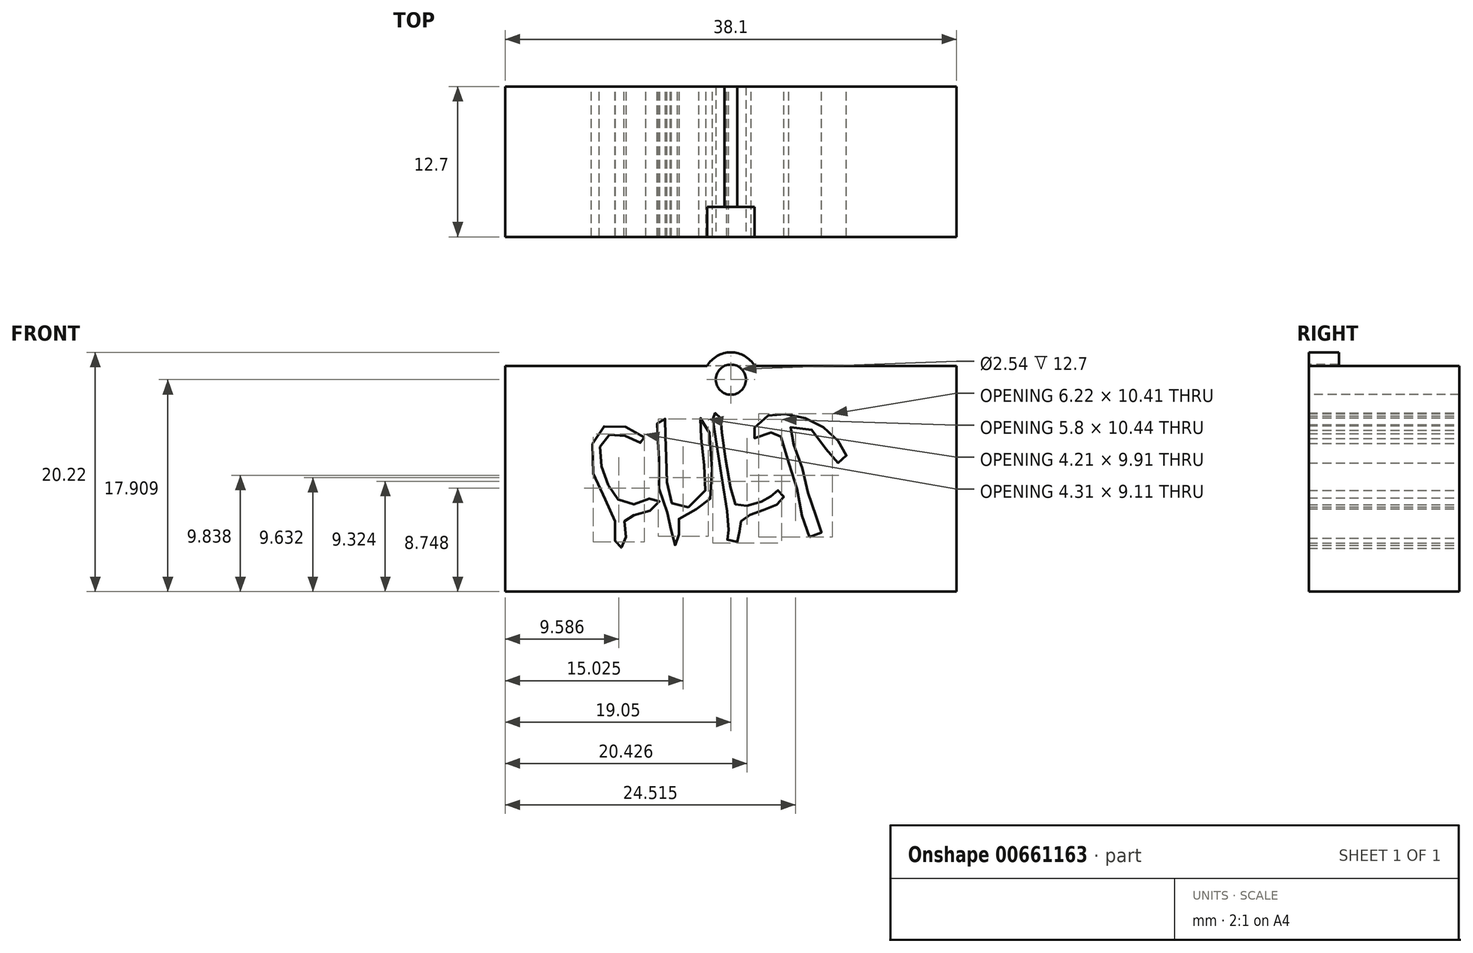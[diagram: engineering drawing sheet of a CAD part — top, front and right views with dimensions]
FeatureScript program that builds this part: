
annotation { "Feature Type Name" : "Feature", "Feature Type Description" : "" }
export const myFeature = defineFeature(function(context is Context, id is Id, definition is map)
    precondition{}
    {
        {
            var Q0;
            Q0=qCreatedBy(makeId("Front.planeOp"),FACE);
            var sketch = newSketch(context, id + "F0", { "sketchPlane" : qUnion([Q0])});
            skLineSegment(sketch, "E0.bottom", {"start": v(19.05, 9.53) * mm, "end": v(-19.05, 9.53) * mm});
            skLineSegment(sketch, "E0.top", {"start": v(19.05, -9.53) * mm, "end": v(-19.05, -9.53) * mm});
            skLineSegment(sketch, "E0.left", {"start": v(19.05, 9.53) * mm, "end": v(19.05, -9.53) * mm});
            skLineSegment(sketch, "E0.right", {"start": v(-19.05, 9.53) * mm, "end": v(-19.05, -9.53) * mm});
            skPoint(sketch, "E0.middle", {"position": v(0, 0) * mm});
            skSolve(sketch);
        }
        {
            var Q0;
            Q0=makeQuery(id+"F0.imprint","IMPRINT",FACE,{"disambiguationData":[TD([[makeQuery(id+"F0.imprint","IMPRINT",EDGE,{"derivedFrom":sQuery(id+"F0.wireOp",EDGE,"E0.bottom")}),1.0]])]});
            extrude(context, id + "F1", {"entities" : qUnion([Q0]), "depth" : 12.7 * mm, "offsetDistance" : 25.4 * mm});
        }
        {
            var Q0;
            Q0=makeQuery(id+"F1.opExtrude","CAP_FACE",FACE,{"disambiguationData":[OSD([sQuery(id+"F0.wireOp",EDGE,"E0.bottom"),sQuery(id+"F0.wireOp",EDGE,"E0.top"),sQuery(id+"F0.wireOp",EDGE,"E0.left"),sQuery(id+"F0.wireOp",EDGE,"E0.right")])],"isStart":false});
            var sketch = newSketch(context, id + "F2", { "sketchPlane" : qUnion([Q0])});
            skFitSpline(sketch, "E1", {"points": [v(-7.3, 3.52) * mm, v(-9.58, 4.55) * mm, v(-11.33, 3.88) * mm, v(-11.5, 0) * mm, v(-9.86, -3.22) * mm, v(-9.78, -5.25) * mm, v(-9.5, -5.85) * mm, v(-8.9, -5.53) * mm, v(-8.9, -4.61) * mm, v(-8.94, -3.42) * mm, v(-8.34, -3.1) * mm, v(-7.07, -2.78) * mm, v(-6, -2.06) * mm, v(-6.4, -1.63) * mm, v(-7.1, -1.74) * mm, v(-8.54, -2.18) * mm, v(-9.78, -1.47) * mm, v(-10.58, 0) * mm, v(-11.1, 2.04) * mm, v(-10.66, 3.48) * mm, v(-9.46, 3.8) * mm, v(-8.19, 3.28) * mm, v(-7.27, 3.04) * mm, v(-7.3, 3.52) * mm]});
            skSolve(sketch);
        }
        {
            var Q0;
            Q0=makeQuery(id+"F2.imprint","IMPRINT",FACE,{"disambiguationData":[TD([[makeQuery(id+"F2.imprint","IMPRINT",EDGE,{"derivedFrom":sQuery(id+"F2.wireOp",EDGE,"E1")}),1.0]])]});
            extrude(context, id + "F3", {"entities" : qUnion([Q0]), "operationType" : NewBodyOperationType.REMOVE, "oppositeDirection" : true, "depth" : 25.4 * mm, "offsetDistance" : 25.4 * mm});
        }
        {
            var Q0;
            Q0=makeQuery(id+"F1.opExtrude","CAP_FACE",FACE,{"disambiguationData":[OSD([sQuery(id+"F0.wireOp",EDGE,"E0.bottom"),sQuery(id+"F0.wireOp",EDGE,"E0.top"),sQuery(id+"F0.wireOp",EDGE,"E0.left"),sQuery(id+"F0.wireOp",EDGE,"E0.right")])],"isStart":false});
            var sketch = newSketch(context, id + "F4", { "sketchPlane" : qUnion([Q0])});
            skFitSpline(sketch, "E2", {"points": [v(-5.37, -2.83) * mm, v(-5, -3.96) * mm, v(-5.06, -5.29) * mm, v(-4.5, -5.6) * mm, v(-4.36, -4.95) * mm, v(-4.5, -4.02) * mm, v(-4.22, -3.14) * mm, v(-2.64, -2.47) * mm, v(-1.8, -1.82) * mm, v(-1.62, 1.65) * mm, v(-2.21, 5.06) * mm, v(-2.64, 5.06) * mm, v(-2.47, 3.28) * mm, v(-2.19, 0.5) * mm, v(-2.41, -1.6) * mm, v(-4.38, -2.52) * mm, v(-5.06, -1.88) * mm, v(-5.43, 0) * mm, v(-5.48, 2.24) * mm, v(-5.51, 3.87) * mm, v(-5.48, 4.97) * mm, v(-6.02, 5.28) * mm, v(-6.22, 4.35) * mm, v(-6.16, 3.17) * mm, v(-6.05, 2.44) * mm, v(-6.1, -0.4) * mm, v(-5.37, -2.83) * mm]});
            skSolve(sketch);
        }
        {
            var Q0;
            Q0=makeQuery(id+"F4.imprint","IMPRINT",FACE,{"disambiguationData":[TD([[makeQuery(id+"F4.imprint","IMPRINT",EDGE,{"derivedFrom":sQuery(id+"F4.wireOp",EDGE,"E2")}),1.0]])]});
            extrude(context, id + "F5", {"entities" : qUnion([Q0]), "operationType" : NewBodyOperationType.REMOVE, "oppositeDirection" : true, "depth" : 25.4 * mm, "offsetDistance" : 25.4 * mm});
        }
        {
            var Q0;
            Q0=makeQuery(id+"F1.opExtrude","CAP_FACE",FACE,{"disambiguationData":[OSD([sQuery(id+"F0.wireOp",EDGE,"E0.bottom"),sQuery(id+"F0.wireOp",EDGE,"E0.top"),sQuery(id+"F0.wireOp",EDGE,"E0.left"),sQuery(id+"F0.wireOp",EDGE,"E0.right")])],"isStart":false});
            var sketch = newSketch(context, id + "F6", { "sketchPlane" : qUnion([Q0])});
            skFitSpline(sketch, "E3", {"points": [v(-1.53, 5.01) * mm, v(-0.51, -1.6) * mm, v(-0.23, -4.51) * mm, v(-0.31, -5.1) * mm, v(0.42, -5.41) * mm, v(0.73, -4.74) * mm, v(0.76, -4.06) * mm, v(0.98, -3.38) * mm, v(1.89, -2.93) * mm, v(3.24, -2.45) * mm, v(4.25, -1.92) * mm, v(4.45, -1.36) * mm, v(4, -0.96) * mm, v(3.52, -1.3) * mm, v(3.04, -1.75) * mm, v(1.86, -2.14) * mm, v(0.59, -2.31) * mm, v(0, -0.9) * mm, v(-0.76, 4.06) * mm, v(-0.9, 5.24) * mm, v(-1.22, 5.58) * mm, v(-1.53, 5.4) * mm, v(-1.53, 5.01) * mm]});
            skSolve(sketch);
        }
        {
            var Q0;
            Q0=makeQuery(id+"F6.imprint","IMPRINT",FACE,{"disambiguationData":[TD([[makeQuery(id+"F6.imprint","IMPRINT",EDGE,{"derivedFrom":sQuery(id+"F6.wireOp",EDGE,"E3")}),1.0]])]});
            extrude(context, id + "F7", {"entities" : qUnion([Q0]), "operationType" : NewBodyOperationType.REMOVE, "oppositeDirection" : true, "depth" : 25.4 * mm, "offsetDistance" : 25.4 * mm});
        }
        {
            var Q0;
            Q0=makeQuery(id+"F1.opExtrude","CAP_FACE",FACE,{"disambiguationData":[OSD([sQuery(id+"F0.wireOp",EDGE,"E0.bottom"),sQuery(id+"F0.wireOp",EDGE,"E0.top"),sQuery(id+"F0.wireOp",EDGE,"E0.left"),sQuery(id+"F0.wireOp",EDGE,"E0.right")])],"isStart":false});
            var sketch = newSketch(context, id + "F8", { "sketchPlane" : qUnion([Q0])});
            skFitSpline(sketch, "E4", {"points": [v(6.64, -4.9) * mm, v(7.58, -4.7) * mm, v(7.35, -3.52) * mm, v(6.4, -0.73) * mm, v(5.55, 2.35) * mm, v(4.98, 4.3) * mm, v(7.16, 3.92) * mm, v(8.48, 1.69) * mm, v(9.53, 1.4) * mm, v(9.72, 2.21) * mm, v(8.67, 3.59) * mm, v(7.1, 4.82) * mm, v(5.02, 5.39) * mm, v(3.37, 5.43) * mm, v(2.09, 4.44) * mm, v(1.75, 3.54) * mm, v(3.03, 3.63) * mm, v(3.84, 4.1) * mm, v(4.88, 1.36) * mm, v(5.83, -1.96) * mm, v(6.64, -4.9) * mm]});
            skSolve(sketch);
        }
        {
            var Q0;
            Q0=makeQuery(id+"F8.imprint","IMPRINT",FACE,{"disambiguationData":[TD([[makeQuery(id+"F8.imprint","IMPRINT",EDGE,{"derivedFrom":sQuery(id+"F8.wireOp",EDGE,"E4")}),1.0]])]});
            extrude(context, id + "F9", {"entities" : qUnion([Q0]), "operationType" : NewBodyOperationType.REMOVE, "oppositeDirection" : true, "depth" : 25.4 * mm, "offsetDistance" : 25.4 * mm});
        }
        {
            var Q0;
            Q0=makeQuery(id+"F1.opExtrude","CAP_FACE",FACE,{"disambiguationData":[OSD([sQuery(id+"F0.wireOp",EDGE,"E0.bottom"),sQuery(id+"F0.wireOp",EDGE,"E0.top"),sQuery(id+"F0.wireOp",EDGE,"E0.left"),sQuery(id+"F0.wireOp",EDGE,"E0.right")])],"isStart":false});
            var sketch = newSketch(context, id + "F10", { "sketchPlane" : qUnion([Q0])});
            skCircle(sketch, "E5", {"center": v(0, 8.38) * mm, "radius": 2.3 * mm});
            skSolve(sketch);
        }
        {
            var Q0;
            {var subQ0=sQuery(id+"F10.wireOp",EDGE,"E5");var subQ1=makeQuery(id+"F1.opExtrude","CAP_EDGE",EDGE,{"disambiguationData":[OSD([sQuery(id+"F0.wireOp",EDGE,"E0.bottom")])],"isStart":false});var subQ2=makeQuery(id+"F10.imprint","INTERSECT",VERTEX,{"disambiguationData":[OD(0.0)],"derivedFrom":[subQ1,subQ0]});Q0=makeQuery(id+"F10.imprint","IMPRINT",FACE,{"disambiguationData":[TD([[makeQuery(id+"F10.imprint","IMPRINT",EDGE,{"disambiguationData":[TD([[subQ2,-1.0]])],"derivedFrom":subQ0}),1.0]])]});}
            extrude(context, id + "F11", {"entities" : qUnion([Q0]), "operationType" : NewBodyOperationType.ADD, "oppositeDirection" : true, "depth" : 2.54 * mm, "offsetDistance" : 25.4 * mm});
        }
        {
            var Q0;
            {var subQ0=sQuery(id+"F0.wireOp",EDGE,"E0.bottom");Q0=makeQuery(id+"F11.boolean.opBoolean","MERGE",FACE,{"derivedFrom":[makeQuery(id+"F1.opExtrude","CAP_FACE",FACE,{"disambiguationData":[OSD([subQ0,sQuery(id+"F0.wireOp",EDGE,"E0.top"),sQuery(id+"F0.wireOp",EDGE,"E0.left"),sQuery(id+"F0.wireOp",EDGE,"E0.right")])],"isStart":false}),makeQuery(id+"F11.opExtrude","CAP_FACE",FACE,{"disambiguationData":[OSD([subQ0,sQuery(id+"F10.wireOp",EDGE,"E5")])],"isStart":true})]});}
            var sketch = newSketch(context, id + "F12", { "sketchPlane" : qUnion([Q0])});
            skCircle(sketch, "E6", {"center": v(0, 8.38) * mm, "radius": 1.27 * mm});
            skSolve(sketch);
        }
        {
            var Q0;
            Q0=makeQuery(id+"F12.imprint","IMPRINT",FACE,{"disambiguationData":[TD([[makeQuery(id+"F12.imprint","IMPRINT",EDGE,{"derivedFrom":sQuery(id+"F12.wireOp",EDGE,"E6")}),1.0]])]});
            extrude(context, id + "F13", {"entities" : qUnion([Q0]), "operationType" : NewBodyOperationType.REMOVE, "oppositeDirection" : true, "depth" : 25.4 * mm, "offsetDistance" : 25.4 * mm});
        }
    });
